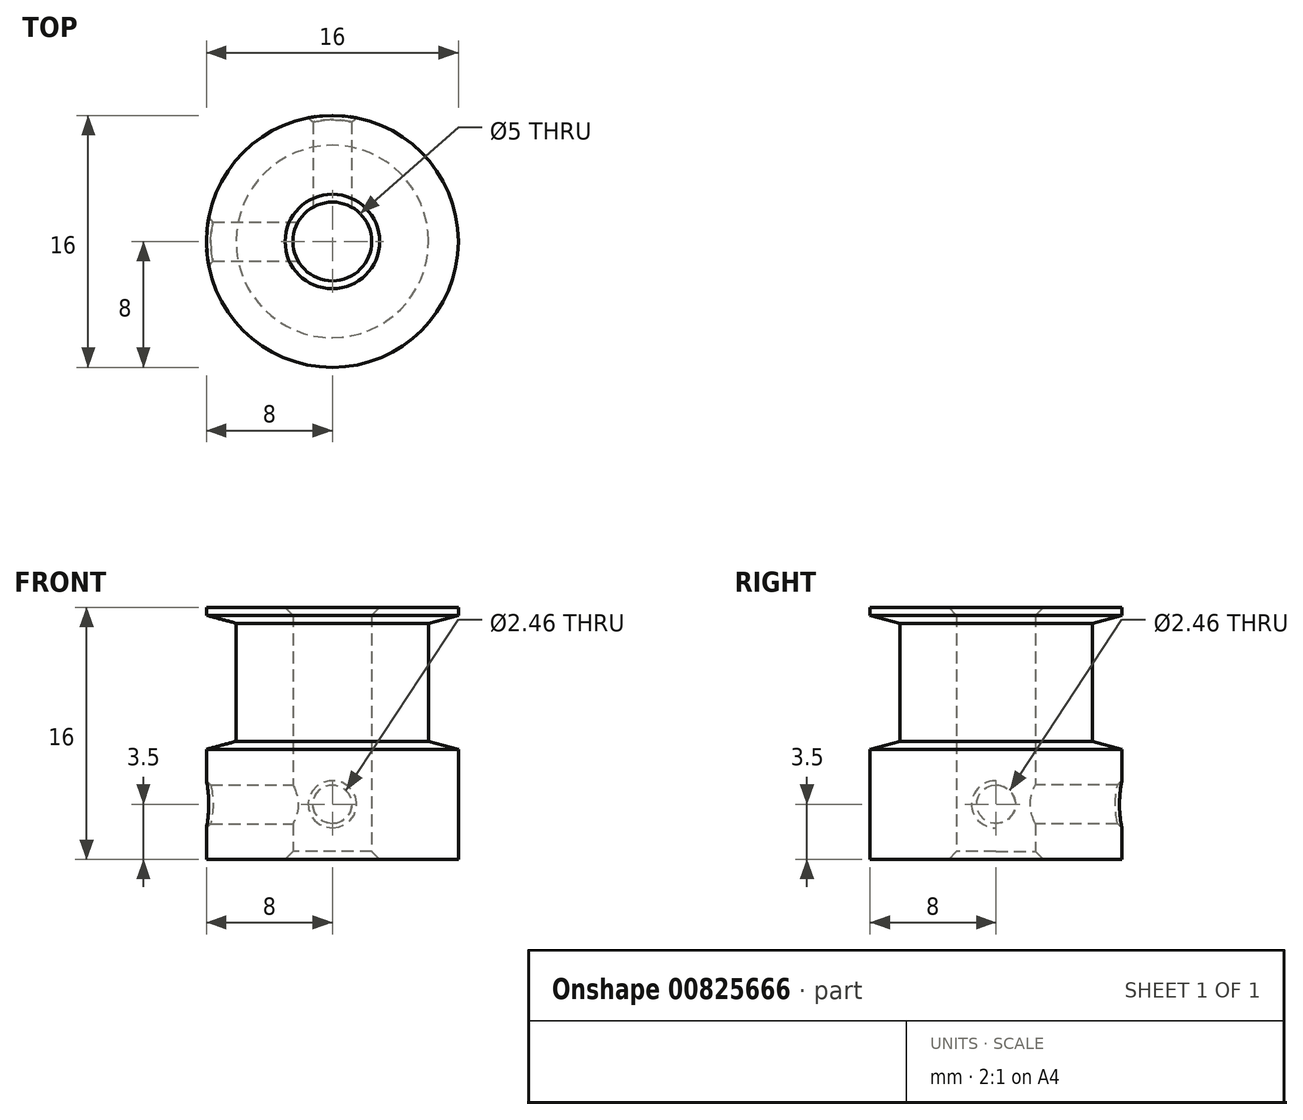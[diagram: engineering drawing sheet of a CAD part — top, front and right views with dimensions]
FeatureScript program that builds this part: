
annotation { "Feature Type Name" : "Feature", "Feature Type Description" : "" }
export const myFeature = defineFeature(function(context is Context, id is Id, definition is map)
    precondition{}
    {
        {
            var Q0;
            Q0=qCreatedBy(makeId("Front.planeOp"),FACE);
            var sketch = newSketch(context, id + "F0", { "sketchPlane" : qUnion([Q0])});
            skLineSegment(sketch, "E0", {"start": v(0, 0) * mm, "end": v(0, 26.28) * mm, "construction": true});
            skLineSegment(sketch, "E1", {"start": v(2.5, 0) * mm, "end": v(2.5, 16) * mm});
            skLineSegment(sketch, "E2", {"start": v(2.5, 16) * mm, "end": v(8, 16) * mm});
            skLineSegment(sketch, "E3", {"start": v(8, 16) * mm, "end": v(8, 15.5) * mm});
            skLineSegment(sketch, "E4", {"start": v(8, 15.5) * mm, "end": v(6.1, 15) * mm});
            skLineSegment(sketch, "E5", {"start": v(6.1, 15) * mm, "end": v(6.1, 7.5) * mm});
            skLineSegment(sketch, "E6", {"start": v(6.11, 7.5) * mm, "end": v(8, 7) * mm});
            skLineSegment(sketch, "E7", {"start": v(8, 7) * mm, "end": v(8, 0) * mm});
            skLineSegment(sketch, "E8", {"start": v(8, 0) * mm, "end": v(2.5, 0) * mm});
            skSolve(sketch);
        }
        {
            var Q0;
            Q0=qSketchRegion(id+"F0",true);
            var Q1;
            Q1=sQuery(id+"F0.wireOp",EDGE,"E0");
            revolve(context, id + "F1", {"entities" : qUnion([Q0]), "axis" : qUnion([Q1]), "revolveType" : RevolveType.FULL});
        }
        {
            var Q0;
            Q0=qCreatedBy(makeId("Front.planeOp"),FACE);
            var sketch = newSketch(context, id + "F2", { "sketchPlane" : qUnion([Q0])});
            skCircle(sketch, "E9", {"center": v(0, 3.5) * mm, "radius": 1.23 * mm});
            skSolve(sketch);
        }
        {
            var Q0;
            Q0=qSketchRegion(id+"F2",true);
            extrude(context, id + "F3", {"entities" : qUnion([Q0]), "operationType" : NewBodyOperationType.REMOVE, "oppositeDirection" : true, "depth" : 25 * mm});
        }
        {
            var Q0;
            Q0=qCreatedBy(makeId("Right.planeOp"),FACE);
            var sketch = newSketch(context, id + "F4", { "sketchPlane" : qUnion([Q0])});
            skCircle(sketch, "E10", {"center": v(0, 3.5) * mm, "radius": 1.23 * mm});
            skSolve(sketch);
        }
        {
            var Q0;
            Q0=qSketchRegion(id+"F4",true);
            extrude(context, id + "F5", {"entities" : qUnion([Q0]), "operationType" : NewBodyOperationType.REMOVE, "oppositeDirection" : true, "depth" : 25 * mm});
        }
        {
            var Q0;
            Q0=makeQuery(id+"F3.boolean.opBoolean","INTERSECT",EDGE,{"derivedFrom":[makeQuery(id+"F1.opRevolve","SWEPT_FACE",FACE,{"disambiguationData":[OSD([sQuery(id+"F0.wireOp",EDGE,"E7")])]}),makeQuery(id+"F3.opExtrude","SWEPT_FACE",FACE,{"disambiguationData":[OSD([sQuery(id+"F2.wireOp",EDGE,"E9")])]})]});
            var Q1;
            Q1=makeQuery(id+"F5.boolean.opBoolean","INTERSECT",EDGE,{"derivedFrom":[makeQuery(id+"F1.opRevolve","SWEPT_FACE",FACE,{"disambiguationData":[OSD([sQuery(id+"F0.wireOp",EDGE,"E7")])]}),makeQuery(id+"F5.opExtrude","SWEPT_FACE",FACE,{"disambiguationData":[OSD([sQuery(id+"F4.wireOp",EDGE,"E10")])]})]});
            chamfer(context, id + "F6", {"entities" : qUnion([Q0, Q1]), "width" : 0.27 * mm, "tangentPropagation" : true});
        }
        {
            var Q0;
            Q0=makeQuery(id+"F1.opRevolve","SWEPT_EDGE",EDGE,{"disambiguationData":[OSD([sQuery(id+"F0.wireOp",EDGE,"E1"),sQuery(id+"F0.wireOp",EDGE,"E2")])]});
            var Q1;
            Q1=makeQuery(id+"F1.opRevolve","SWEPT_EDGE",EDGE,{"disambiguationData":[OSD([sQuery(id+"F0.wireOp",EDGE,"E1"),sQuery(id+"F0.wireOp",EDGE,"E8")])]});
            chamfer(context, id + "F7", {"entities" : qUnion([Q0, Q1]), "width" : 0.5 * mm, "tangentPropagation" : true});
        }
    });
